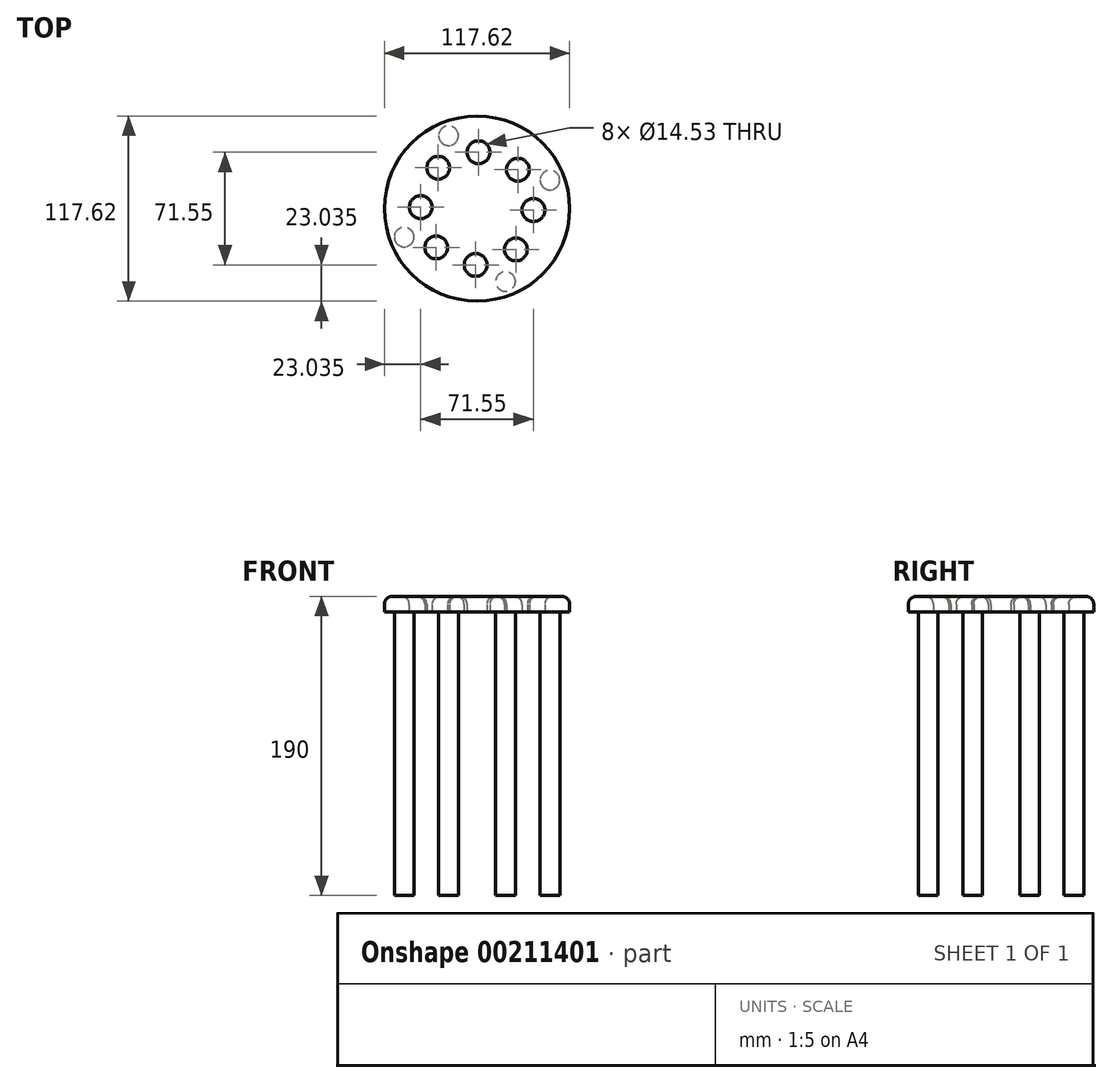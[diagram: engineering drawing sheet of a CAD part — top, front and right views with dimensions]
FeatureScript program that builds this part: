
annotation { "Feature Type Name" : "Feature", "Feature Type Description" : "" }
export const myFeature = defineFeature(function(context is Context, id is Id, definition is map)
    precondition{}
    {
        {
            var Q0;
            Q0=qCreatedBy(makeId("Top.planeOp"),FACE);
            var sketch = newSketch(context, id + "F0", { "sketchPlane" : qUnion([Q0])});
            skCircle(sketch, "E0", {"center": v(0, 0) * mm, "radius": 58.8 * mm});
            skCircle(sketch, "E1", {"center": v(-24.66, 25.93) * mm, "radius": 7.26 * mm});
            skCircle(sketch, "E2.1.0", {"center": v(-35.78, 0.9) * mm, "radius": 7.26 * mm});
            skCircle(sketch, "E2.2.0", {"center": v(-25.93, -24.66) * mm, "radius": 7.26 * mm});
            skCircle(sketch, "E2.3.0", {"center": v(-0.9, -35.78) * mm, "radius": 7.26 * mm});
            skCircle(sketch, "E2.4.0", {"center": v(24.66, -25.93) * mm, "radius": 7.26 * mm});
            skCircle(sketch, "E2.5.0", {"center": v(35.78, -0.9) * mm, "radius": 7.26 * mm});
            skCircle(sketch, "E2.6.0", {"center": v(25.93, 24.66) * mm, "radius": 7.26 * mm});
            skCircle(sketch, "E2.7.0", {"center": v(0.9, 35.78) * mm, "radius": 7.26 * mm});
            skSolve(sketch);
        }
        {
            var Q0;
            Q0=makeQuery(id+"F0.imprint","IMPRINT",FACE,{"disambiguationData":[TD([[makeQuery(id+"F0.imprint","IMPRINT",EDGE,{"derivedFrom":sQuery(id+"F0.wireOp",EDGE,"E0")}),1.0]])]});
            extrude(context, id + "F1", {"entities" : qUnion([Q0]), "depth" : 10 * mm});
        }
        {
            var Q0;
            Q0=makeQuery(id+"F1.opExtrude","CAP_EDGE",EDGE,{"disambiguationData":[OSD([sQuery(id+"F0.wireOp",EDGE,"E0")])],"isStart":false});
            fillet(context, id + "F2", {"entities" : qUnion([Q0]), "radius" : 5 * mm, "tangentPropagation" : true, "allowEdgeOverflow" : false});
        }
        {
            var Q0;
            Q0=makeQuery(id+"F1.opExtrude","CAP_FACE",FACE,{"disambiguationData":[OSD([sQuery(id+"F0.wireOp",EDGE,"E0"),sQuery(id+"F0.wireOp",EDGE,"E1"),sQuery(id+"F0.wireOp",EDGE,"E2.1.0"),sQuery(id+"F0.wireOp",EDGE,"E2.2.0"),sQuery(id+"F0.wireOp",EDGE,"E2.3.0"),sQuery(id+"F0.wireOp",EDGE,"E2.4.0"),sQuery(id+"F0.wireOp",EDGE,"E2.5.0"),sQuery(id+"F0.wireOp",EDGE,"E2.6.0"),sQuery(id+"F0.wireOp",EDGE,"E2.7.0")])],"isStart":true});
            var sketch = newSketch(context, id + "F3", { "sketchPlane" : qUnion([Q0])});
            skCircle(sketch, "E3", {"center": v(18.1, 46.3) * mm, "radius": 6.25 * mm});
            skCircle(sketch, "E4.1.0", {"center": v(-46.3, 18.1) * mm, "radius": 6.25 * mm});
            skCircle(sketch, "E4.2.0", {"center": v(-18.1, -46.3) * mm, "radius": 6.25 * mm});
            skCircle(sketch, "E4.3.0", {"center": v(46.3, -18.1) * mm, "radius": 6.25 * mm});
            skPoint(sketch, "E4.center", {"position": v(0, 0) * mm});
            skSolve(sketch);
        }
        {
            var Q0;
            Q0 = qSketchRegion(id + "F3", true);
            extrude(context, id + "F4", {"entities" : qUnion([Q0]), "operationType" : NewBodyOperationType.ADD, "depth" : 180 * mm});
        }
        {
            var Q0;
            Q0=makeQuery(id+"F1.opExtrude","CAP_FACE",FACE,{"disambiguationData":[OSD([sQuery(id+"F0.wireOp",EDGE,"E0"),sQuery(id+"F0.wireOp",EDGE,"E1"),sQuery(id+"F0.wireOp",EDGE,"E2.1.0"),sQuery(id+"F0.wireOp",EDGE,"E2.2.0"),sQuery(id+"F0.wireOp",EDGE,"E2.3.0"),sQuery(id+"F0.wireOp",EDGE,"E2.4.0"),sQuery(id+"F0.wireOp",EDGE,"E2.5.0"),sQuery(id+"F0.wireOp",EDGE,"E2.6.0"),sQuery(id+"F0.wireOp",EDGE,"E2.7.0")])],"isStart":false});
            fillet(context, id + "F5", {"entities" : qUnion([Q0]), "radius" : 5 * mm, "tangentPropagation" : true, "allowEdgeOverflow" : false});
        }
    });
